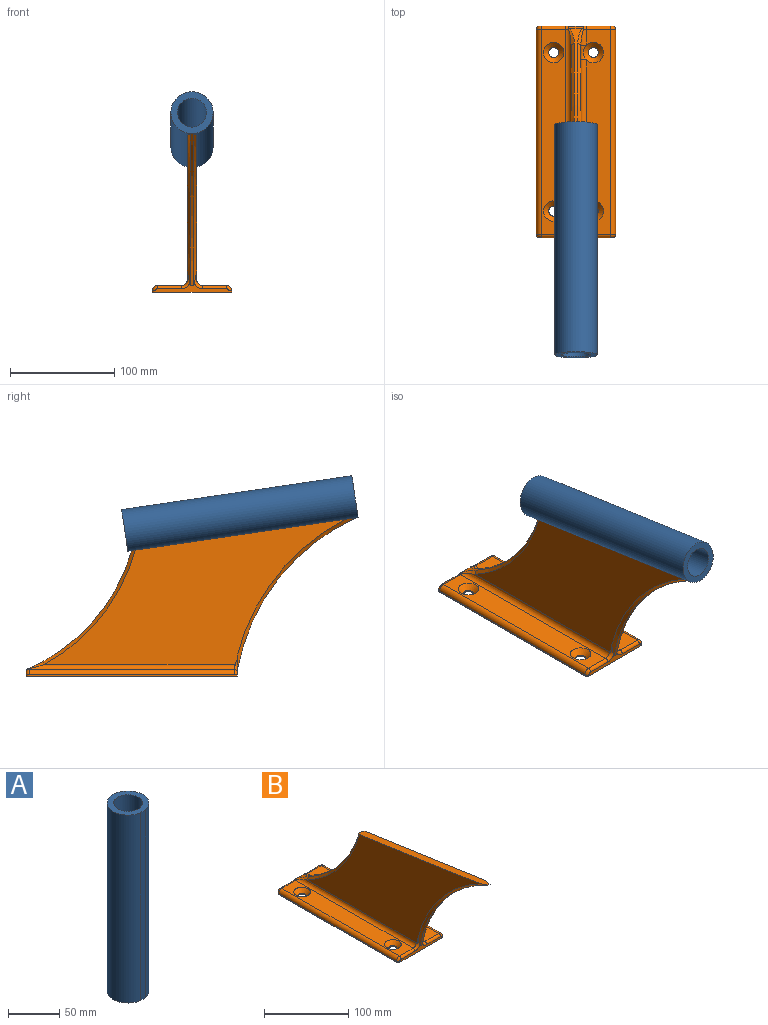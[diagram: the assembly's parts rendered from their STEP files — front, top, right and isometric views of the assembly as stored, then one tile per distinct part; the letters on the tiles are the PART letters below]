
ASSEMBLY  parts=2 mates=1
PART A: 5 faces, bbox 40.6x40.5x223.5 mm
  f0: cylinder r=20.32mm len=223.52mm, axis (0,0,-1), area 27112.6mm2, adj f2,f3,f4
  f1: cylinder r=13.97mm len=223.52mm, axis (0,0,-1), area 19619.7mm2, adj f3,f4
  f2: plane 223.52x6.35mm, normal (0.03,-1,0), area 1419.4mm2, adj f0,f3,f4
  f3: plane 40.64x40.47mm, normal (0,0,1), area 683mm2, adj f0,f1,f2
  f4: plane 40.64x40.47mm, normal (0,0,-1), area 683mm2, adj f0,f1,f2
PART B: 55 faces, bbox 76.4x317.7x155.4 mm
  f0: cone r=202.68mm half-angle=45deg, axis (-1,0,0), area 788mm2, adj f2,f3,f6,f8,f34
  f1: cone r=199.63mm half-angle=45deg, axis (1,0,0), area 0mm2, adj f5,f30
  f2: plane 216.09x31.94mm, normal (0,0.15,0.99), area 2036.4mm2, adj f0,f3,f4,f5,f6,f46,f52,f53
  f3: cylinder r=199.63mm len=146.05mm, axis (-1,0,0), area 661.4mm2, adj f0,f2,f8,f53
  f4: cylinder r=175.64mm len=113.52mm, axis (-1,0,0), area 602.6mm2, adj f2,f46,f47,f49,f51,f52
  f5: plane 289.77x140.61mm, normal (1,0,0), area 18910mm2, adj f1,f2,f25,f26,f27,f28,f29,f30
  f6: plane 289.8x140.6mm, normal (-1,0,0), area 18896mm2, adj f0,f2,f24,f34,f52,f54
  f7: plane 197.1x23.18mm, normal (0,0,1), area 4017.6mm2, adj f18,f20,f23,f25,f27,f29,f31,f43
  f8: plane 70.11x8.78mm, normal (0,-1,0), area 266.7mm2, adj f0,f3,f16,f30,f31,f32,f33,f34
  f9: plane 197.1x1.27mm, normal (-1,0,0), area 250.3mm2, adj f16,f22,f37,f41
  f10: plane 70.1x4.33mm, normal (0,1,0), area 244.4mm2, adj f16,f38,f39,f40,f41,f42,f43,f44
  f11: cylinder r=4.78mm len=9.55mm, axis (0,0,1), area 38.1mm2, adj f16,f19
  f12: cylinder r=4.78mm len=9.55mm, axis (0,0,1), area 38.1mm2, adj f16,f20
  f13: cylinder r=4.78mm len=9.55mm, axis (0,0,1), area 38.1mm2, adj f16,f18
  f14: plane 197.1x1.27mm, normal (1,0,0), area 250.3mm2, adj f16,f23,f33,f45
  f15: cylinder r=4.78mm len=9.55mm, axis (0,0,1), area 38.1mm2, adj f16,f21
  f16: plane 203.2x76.2mm, normal (0,0,-1), area 15189.3mm2, adj f8,f9,f10,f11,f12,f13,f14,f15
  f17: plane 197.1x23.18mm, normal (0,0,1), area 3958.1mm2, adj f19,f21,f22,f24,f35,f39
  f18: cone r=9.86mm half-angle=45deg, axis (0,0,1), area 330.2mm2, adj f7,f13,f28
  f19: cone r=9.86mm half-angle=45deg, axis (0,0,1), area 330.2mm2, adj f11,f17
  f20: cone r=9.86mm half-angle=45deg, axis (0,0,1), area 330.2mm2, adj f7,f12,f26
  f21: cone r=9.86mm half-angle=45deg, axis (0,0,1), area 330.2mm2, adj f15,f17
  f22: cylinder r=5.08mm len=197.1mm, axis (0,1,0), area 1572.8mm2, adj f9,f17,f36,f40
  f23: cylinder r=5.08mm len=197.1mm, axis (0,-1,0), area 1572.8mm2, adj f7,f14,f32,f44
  f24: cylinder r=5.08mm len=197.1mm, axis (0,1,0), area 1533.2mm2, adj f6,f17,f34,f38,f51
  f25: cylinder r=5.08mm len=15.24mm, axis (0,-1,0), area 121.6mm2, adj f5,f7,f26,f30
  f26: bspline ~14.22x5.08mm, area 83.3mm2, adj f5,f20,f25,f27
  f27: cylinder r=5.08mm len=138.18mm, axis (0,-1,0), area 1102.7mm2, adj f5,f7,f26,f28
  f28: bspline ~14.22x5.08mm, area 83.3mm2, adj f5,f18,f27,f29
  f29: cylinder r=5.08mm len=15.24mm, axis (0,-1,0), area 84.8mm2, adj f5,f7,f28,f42,f47
  f30: torus R=8.13mm, axis (0,1,0), area 53.9mm2, adj f1,f5,f8,f25,f31,f53
  f31: cylinder r=3.05mm len=23.18mm, axis (-1,0,0), area 111mm2, adj f7,f8,f30,f32
  f32: torus R=2.03mm, axis (0,1,0), area 29.9mm2, adj f8,f23,f31,f33
  f33: cylinder r=3.05mm len=3.05mm, axis (0,0,-1), area 6.1mm2, adj f8,f14,f16,f32
  f34: torus R=8.13mm, axis (0,1,0), area 53.9mm2, adj f0,f6,f8,f24,f35,f54
  f35: cylinder r=3.05mm len=23.18mm, axis (-1,0,0), area 111mm2, adj f8,f17,f34,f36
  f36: torus R=2.03mm, axis (0,1,0), area 29.9mm2, adj f8,f22,f35,f37
  f37: cylinder r=3.05mm len=3.05mm, axis (0,0,1), area 6.1mm2, adj f8,f9,f16,f36
  f38: torus R=8.13mm, axis (0,1,0), area 15mm2, adj f10,f24,f39,f50
  f39: cylinder r=3.05mm len=23.18mm, axis (1,0,0), area 111mm2, adj f10,f17,f38,f40
  f40: torus R=2.03mm, axis (0,1,0), area 29.9mm2, adj f10,f22,f39,f41
  f41: cylinder r=3.05mm len=3.05mm, axis (0,0,-1), area 6.1mm2, adj f9,f10,f16,f40
  f42: torus R=8.13mm, axis (0,1,0), area 15mm2, adj f10,f29,f43,f48
  f43: cylinder r=3.05mm len=23.18mm, axis (1,0,0), area 111mm2, adj f7,f10,f42,f44
  f44: torus R=2.03mm, axis (0,1,0), area 29.9mm2, adj f10,f23,f43,f45
  f45: cylinder r=3.05mm len=3.05mm, axis (0,0,1), area 6.1mm2, adj f10,f14,f16,f44
  f46: cone r=175.64mm half-angle=45deg, axis (1,0,0), area 612.5mm2, adj f2,f4,f5,f47
  f47: bspline ~15.87x7.12mm, area 51.9mm2, adj f4,f29,f46,f48
  f48: bspline ~3.05x2.8mm, area 3.8mm2, adj f42,f47,f49
  f49: plane 11.78x2.8mm, normal (0,0.83,0.55), area 39.5mm2, adj f4,f10,f48,f50
  f50: bspline ~3.05x2.8mm, area 3.8mm2, adj f38,f49,f51
  f51: bspline ~15.87x7.12mm, area 51.9mm2, adj f4,f24,f50,f52
  f52: cone r=178.69mm half-angle=45deg, axis (-1,0,0), area 612.5mm2, adj f2,f4,f6,f51
  f53: cone r=199.63mm half-angle=45deg, axis (1,0,0), area 788.1mm2, adj f2,f3,f5,f8,f30
  f54: cone r=202.68mm half-angle=45deg, axis (-1,0,0), area 0mm2, adj f6,f34
PLACE A rot(axis=(1,0.01,-0.02),81.6deg) t=(-74.07,29.02,91.35)mm
PLACE B t=(-78.83,22.37,-42.26)mm
MATE fastened A.f2 <-> B.f2  axis (0,-0.15,-0.99) through (-74.07,-84.47,87.75)mm
